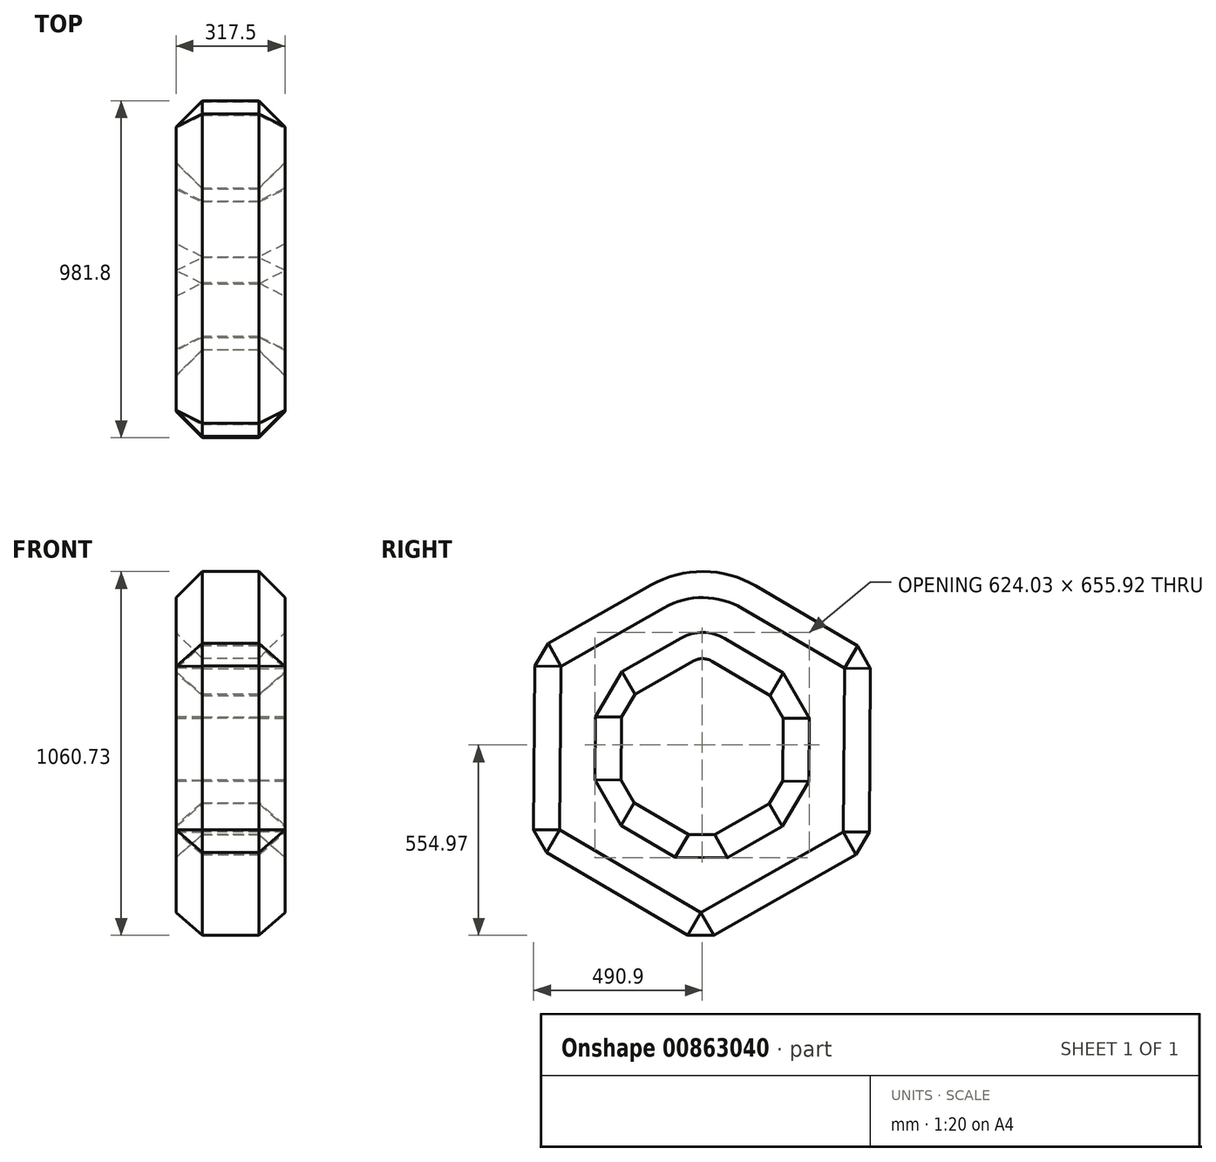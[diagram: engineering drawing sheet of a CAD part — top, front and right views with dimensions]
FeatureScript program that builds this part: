
annotation { "Feature Type Name" : "Feature", "Feature Type Description" : "" }
export const myFeature = defineFeature(function(context is Context, id is Id, definition is map)
    precondition{}
    {
        {
            var Q0;
            Q0=qCreatedBy(makeId("Right.planeOp"),FACE);
            var sketch = newSketch(context, id + "F0", { "sketchPlane" : qUnion([Q0])});
            skCircle(sketch, "E0.cCircle", {"center": v(0, 0) * mm, "radius": 235.14 * mm, "construction": true});
            skLineSegment(sketch, "E0.0", {"start": v(234.13, -137.5) * mm, "end": v(-2.02, -271.51) * mm});
            skLineSegment(sketch, "E0.1", {"start": v(-2.02, -271.51) * mm, "end": v(-236.15, -134) * mm});
            skLineSegment(sketch, "E0.2", {"start": v(-236.15, -134) * mm, "end": v(-234.13, 137.5) * mm});
            skLineSegment(sketch, "E0.3", {"start": v(-234.13, 137.5) * mm, "end": v(-23.49, 257.04) * mm});
            skLineSegment(sketch, "E0.4", {"start": v(27.3, 256.66) * mm, "end": v(236.15, 134) * mm});
            skLineSegment(sketch, "E0.5", {"start": v(236.15, 134) * mm, "end": v(234.13, -137.5) * mm});
            skPoint(sketch, "E0.0.midPoint", {"position": v(116.05, -204.5) * mm});
            skPoint(sketch, "E1.visualSharp", {"position": v(2.02, 271.51) * mm});
            skArc(sketch, "E1.filletArc", {"start": v(27.3, 256.66) * mm, "mid": v(1.96, 263.65) * mm, "end": v(-23.49, 257.04) * mm});
            skLineSegment(sketch, "E2.0", {"start": v(487.03, -286.04) * mm, "end": v(-4.2, -564.8) * mm});
            skLineSegment(sketch, "E2.1", {"start": v(491.23, 278.76) * mm, "end": v(487.03, -286.04) * mm});
            skLineSegment(sketch, "E2.2", {"start": v(-491.23, -278.76) * mm, "end": v(-487.03, 286.04) * mm});
            skLineSegment(sketch, "E2.3", {"start": v(-487.03, 286.04) * mm, "end": v(-148.85, 477.94) * mm});
            skArc(sketch, "E2.4", {"start": v(155.94, 475.68) * mm, "mid": v(3.85, 517.65) * mm, "end": v(-148.85, 477.94) * mm});
            skLineSegment(sketch, "E2.5", {"start": v(-4.2, -564.8) * mm, "end": v(-491.23, -278.76) * mm});
            skLineSegment(sketch, "E2.6", {"start": v(155.94, 475.68) * mm, "end": v(491.23, 278.76) * mm});
            skSolve(sketch);
        }
        {
            var Q0;
            Q0=makeQuery(id+"F0.imprint","IMPRINT",FACE,{"disambiguationData":[TD([[makeQuery(id+"F0.imprint","IMPRINT",EDGE,{"derivedFrom":sQuery(id+"F0.wireOp",EDGE,"E0.0")}),1.0]])]});
            var Q1;
            Q1 = qConstructionFilter(qBodyType(qCreatedBy(id + "F0" ,EDGE), BodyType.WIRE), ConstructionObject.NO);
            extrude(context, id + "F1", {"entities" : qUnion([Q0]), "surfaceEntities" : qUnion([Q1]), "depth" : 317.5 * mm, "offsetDistance" : 25.4 * mm});
        }
        {
            var Q0;
            Q0=makeQuery(id+"F1.opExtrude","SWEPT_EDGE",EDGE,{"disambiguationData":[OSD([sQuery(id+"F0.wireOp",EDGE,"E2.0"),sQuery(id+"F0.wireOp",EDGE,"E2.5")])]});
            var Q1;
            Q1=makeQuery(id+"F1.opExtrude","SWEPT_EDGE",EDGE,{"disambiguationData":[OSD([sQuery(id+"F0.wireOp",EDGE,"E2.0"),sQuery(id+"F0.wireOp",EDGE,"E2.1")])]});
            var Q2;
            Q2=makeQuery(id+"F1.opExtrude","SWEPT_EDGE",EDGE,{"disambiguationData":[OSD([sQuery(id+"F0.wireOp",EDGE,"E0.4"),sQuery(id+"F0.wireOp",EDGE,"E0.5")])]});
            var Q3;
            Q3=makeQuery(id+"F1.opExtrude","SWEPT_EDGE",EDGE,{"disambiguationData":[OSD([sQuery(id+"F0.wireOp",EDGE,"E2.2"),sQuery(id+"F0.wireOp",EDGE,"E2.5")])]});
            var Q4;
            Q4=makeQuery(id+"F1.opExtrude","SWEPT_EDGE",EDGE,{"disambiguationData":[OSD([sQuery(id+"F0.wireOp",EDGE,"E2.2"),sQuery(id+"F0.wireOp",EDGE,"E2.3")])]});
            var Q5;
            Q5=makeQuery(id+"F1.opExtrude","CAP_EDGE",EDGE,{"disambiguationData":[OSD([sQuery(id+"F0.wireOp",EDGE,"E2.0")])],"isStart":false});
            var Q6;
            Q6=makeQuery(id+"F1.opExtrude","CAP_EDGE",EDGE,{"disambiguationData":[OSD([sQuery(id+"F0.wireOp",EDGE,"E2.1")])],"isStart":false});
            var Q7;
            Q7=makeQuery(id+"F1.opExtrude","CAP_EDGE",EDGE,{"disambiguationData":[OSD([sQuery(id+"F0.wireOp",EDGE,"E2.2")])],"isStart":true});
            var Q8;
            Q8=makeQuery(id+"F1.opExtrude","CAP_EDGE",EDGE,{"disambiguationData":[OSD([sQuery(id+"F0.wireOp",EDGE,"E0.1")])],"isStart":false});
            var Q9;
            Q9=makeQuery(id+"F1.opExtrude","CAP_EDGE",EDGE,{"disambiguationData":[OSD([sQuery(id+"F0.wireOp",EDGE,"E2.2")])],"isStart":false});
            var Q10;
            Q10=makeQuery(id+"F1.opExtrude","CAP_EDGE",EDGE,{"disambiguationData":[OSD([sQuery(id+"F0.wireOp",EDGE,"E2.4")])],"isStart":false});
            var Q11;
            Q11=makeQuery(id+"F1.opExtrude","CAP_EDGE",EDGE,{"disambiguationData":[OSD([sQuery(id+"F0.wireOp",EDGE,"E2.5")])],"isStart":true});
            var Q12;
            Q12=makeQuery(id+"F1.opExtrude","CAP_EDGE",EDGE,{"disambiguationData":[OSD([sQuery(id+"F0.wireOp",EDGE,"E0.4")])],"isStart":false});
            var Q13;
            Q13=makeQuery(id+"F1.opExtrude","CAP_EDGE",EDGE,{"disambiguationData":[OSD([sQuery(id+"F0.wireOp",EDGE,"E2.5")])],"isStart":false});
            var Q14;
            Q14=makeQuery(id+"F1.opExtrude","CAP_EDGE",EDGE,{"disambiguationData":[OSD([sQuery(id+"F0.wireOp",EDGE,"E2.6")])],"isStart":false});
            var Q15;
            Q15=makeQuery(id+"F1.opExtrude","CAP_EDGE",EDGE,{"disambiguationData":[OSD([sQuery(id+"F0.wireOp",EDGE,"E1.filletArc")])],"isStart":false});
            var Q16;
            Q16=makeQuery(id+"F1.opExtrude","CAP_EDGE",EDGE,{"disambiguationData":[OSD([sQuery(id+"F0.wireOp",EDGE,"E2.0")])],"isStart":true});
            var Q17;
            Q17=makeQuery(id+"F1.opExtrude","SWEPT_EDGE",EDGE,{"disambiguationData":[OSD([sQuery(id+"F0.wireOp",EDGE,"E0.0"),sQuery(id+"F0.wireOp",EDGE,"E0.5")])]});
            var Q18;
            Q18=makeQuery(id+"F1.opExtrude","CAP_EDGE",EDGE,{"disambiguationData":[OSD([sQuery(id+"F0.wireOp",EDGE,"E0.0")])],"isStart":false});
            var Q19;
            Q19=makeQuery(id+"F1.opExtrude","SWEPT_EDGE",EDGE,{"disambiguationData":[OSD([sQuery(id+"F0.wireOp",EDGE,"E0.0"),sQuery(id+"F0.wireOp",EDGE,"E0.1")])]});
            var Q20;
            Q20=makeQuery(id+"F1.opExtrude","CAP_EDGE",EDGE,{"disambiguationData":[OSD([sQuery(id+"F0.wireOp",EDGE,"E0.0")])],"isStart":true});
            var Q21;
            Q21=makeQuery(id+"F1.opExtrude","SWEPT_EDGE",EDGE,{"disambiguationData":[OSD([sQuery(id+"F0.wireOp",EDGE,"E0.4"),sQuery(id+"F0.wireOp",EDGE,"E1.filletArc")])]});
            var Q22;
            Q22=makeQuery(id+"F1.opExtrude","SWEPT_EDGE",EDGE,{"disambiguationData":[OSD([sQuery(id+"F0.wireOp",EDGE,"E0.1"),sQuery(id+"F0.wireOp",EDGE,"E0.2")])]});
            var Q23;
            Q23=makeQuery(id+"F1.opExtrude","SWEPT_EDGE",EDGE,{"disambiguationData":[OSD([sQuery(id+"F0.wireOp",EDGE,"E2.4"),sQuery(id+"F0.wireOp",EDGE,"E2.6")])]});
            var Q24;
            Q24=makeQuery(id+"F1.opExtrude","SWEPT_EDGE",EDGE,{"disambiguationData":[OSD([sQuery(id+"F0.wireOp",EDGE,"E0.2"),sQuery(id+"F0.wireOp",EDGE,"E0.3")])]});
            var Q25;
            Q25=makeQuery(id+"F1.opExtrude","SWEPT_EDGE",EDGE,{"disambiguationData":[OSD([sQuery(id+"F0.wireOp",EDGE,"E0.3"),sQuery(id+"F0.wireOp",EDGE,"E1.filletArc")])]});
            var Q26;
            Q26=makeQuery(id+"F1.opExtrude","SWEPT_EDGE",EDGE,{"disambiguationData":[OSD([sQuery(id+"F0.wireOp",EDGE,"E2.1"),sQuery(id+"F0.wireOp",EDGE,"E2.6")])]});
            var Q27;
            Q27=makeQuery(id+"F1.opExtrude","SWEPT_EDGE",EDGE,{"disambiguationData":[OSD([sQuery(id+"F0.wireOp",EDGE,"E2.3"),sQuery(id+"F0.wireOp",EDGE,"E2.4")])]});
            var Q28;
            Q28=makeQuery(id+"F1.opExtrude","CAP_EDGE",EDGE,{"disambiguationData":[OSD([sQuery(id+"F0.wireOp",EDGE,"E2.1")])],"isStart":true});
            var Q29;
            Q29=makeQuery(id+"F1.opExtrude","CAP_EDGE",EDGE,{"disambiguationData":[OSD([sQuery(id+"F0.wireOp",EDGE,"E0.1")])],"isStart":true});
            var Q30;
            Q30=makeQuery(id+"F1.opExtrude","CAP_EDGE",EDGE,{"disambiguationData":[OSD([sQuery(id+"F0.wireOp",EDGE,"E0.2")])],"isStart":true});
            var Q31;
            Q31=makeQuery(id+"F1.opExtrude","CAP_EDGE",EDGE,{"disambiguationData":[OSD([sQuery(id+"F0.wireOp",EDGE,"E2.3")])],"isStart":true});
            var Q32;
            Q32=makeQuery(id+"F1.opExtrude","CAP_EDGE",EDGE,{"disambiguationData":[OSD([sQuery(id+"F0.wireOp",EDGE,"E0.2")])],"isStart":false});
            var Q33;
            Q33=makeQuery(id+"F1.opExtrude","CAP_EDGE",EDGE,{"disambiguationData":[OSD([sQuery(id+"F0.wireOp",EDGE,"E2.3")])],"isStart":false});
            var Q34;
            Q34=makeQuery(id+"F1.opExtrude","CAP_EDGE",EDGE,{"disambiguationData":[OSD([sQuery(id+"F0.wireOp",EDGE,"E0.3")])],"isStart":true});
            var Q35;
            Q35=makeQuery(id+"F1.opExtrude","CAP_EDGE",EDGE,{"disambiguationData":[OSD([sQuery(id+"F0.wireOp",EDGE,"E2.4")])],"isStart":true});
            var Q36;
            Q36=makeQuery(id+"F1.opExtrude","CAP_EDGE",EDGE,{"disambiguationData":[OSD([sQuery(id+"F0.wireOp",EDGE,"E0.3")])],"isStart":false});
            var Q37;
            Q37=makeQuery(id+"F1.opExtrude","CAP_EDGE",EDGE,{"disambiguationData":[OSD([sQuery(id+"F0.wireOp",EDGE,"E0.4")])],"isStart":true});
            var Q38;
            Q38=makeQuery(id+"F1.opExtrude","CAP_EDGE",EDGE,{"disambiguationData":[OSD([sQuery(id+"F0.wireOp",EDGE,"E0.5")])],"isStart":true});
            var Q39;
            Q39=makeQuery(id+"F1.opExtrude","CAP_EDGE",EDGE,{"disambiguationData":[OSD([sQuery(id+"F0.wireOp",EDGE,"E2.6")])],"isStart":true});
            var Q40;
            Q40=makeQuery(id+"F1.opExtrude","CAP_EDGE",EDGE,{"disambiguationData":[OSD([sQuery(id+"F0.wireOp",EDGE,"E0.5")])],"isStart":false});
            var Q41;
            Q41=makeQuery(id+"F1.opExtrude","CAP_EDGE",EDGE,{"disambiguationData":[OSD([sQuery(id+"F0.wireOp",EDGE,"E1.filletArc")])],"isStart":true});
            chamfer(context, id + "F2", {"entities" : qUnion([Q0, Q1, Q2, Q3, Q4, Q5, Q6, Q7, Q8, Q9, Q10, Q11, Q12, Q13, Q14, Q15, Q16, Q17, Q18, Q19, Q20, Q21, Q22, Q23, Q24, Q25, Q26, Q27, Q28, Q29, Q30, Q31, Q32, Q33, Q34, Q35, Q36, Q37, Q38, Q39, Q40, Q41]), "width" : 76.2 * mm, "tangentPropagation" : true});
        }
    });
